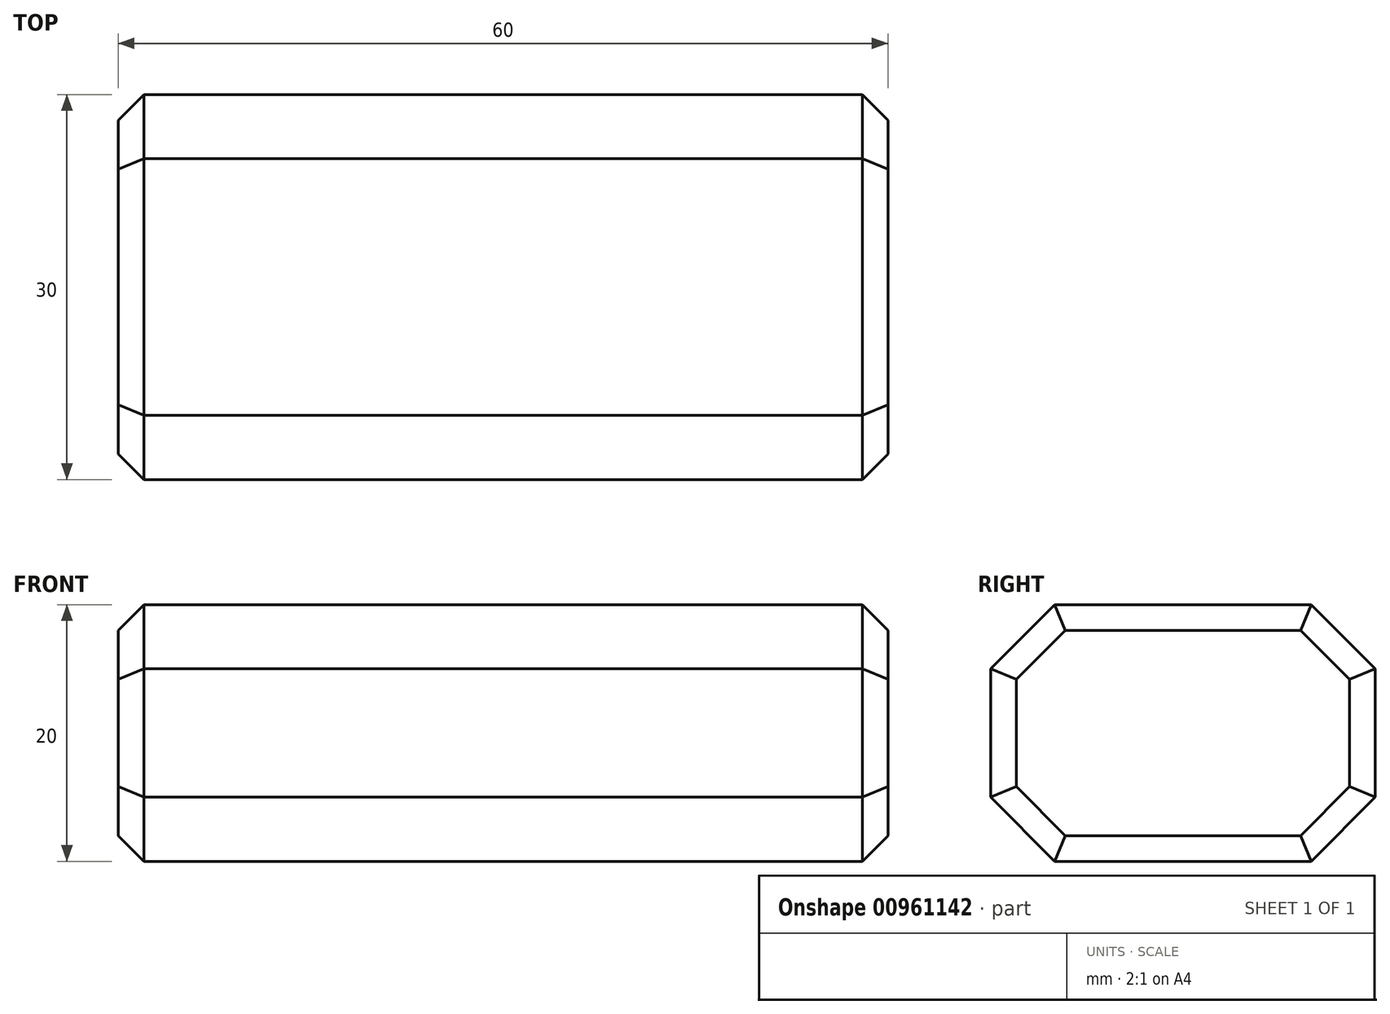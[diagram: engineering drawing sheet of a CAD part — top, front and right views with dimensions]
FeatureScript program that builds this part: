
annotation { "Feature Type Name" : "Feature", "Feature Type Description" : "" }
export const myFeature = defineFeature(function(context is Context, id is Id, definition is map)
    precondition{}
    {
        {
            var Q0;
            Q0=qCreatedBy(makeId("Top.planeOp"),FACE);
            var sketch = newSketch(context, id + "F0", { "sketchPlane" : qUnion([Q0])});
            skLineSegment(sketch, "E0.bottom", {"start": v(-30, 15) * mm, "end": v(30, 15) * mm});
            skLineSegment(sketch, "E0.top", {"start": v(-30, -15) * mm, "end": v(30, -15) * mm});
            skLineSegment(sketch, "E0.left", {"start": v(-30, 15) * mm, "end": v(-30, -15) * mm});
            skLineSegment(sketch, "E0.right", {"start": v(30, 15) * mm, "end": v(30, -15) * mm});
            skLineSegment(sketch, "E1", {"start": v(-30, 0) * mm, "end": v(30, 0) * mm, "construction": true});
            skLineSegment(sketch, "E2", {"start": v(0, 15) * mm, "end": v(0, -15) * mm, "construction": true});
            skPoint(sketch, "E3", {"position": v(0, 0) * mm});
            skSolve(sketch);
        }
        {
            var Q0;
            Q0=qSketchRegion(id+"F0",true);
            extrude(context, id + "F1", {"entities" : qUnion([Q0]), "depth" : 20 * mm, "offsetDistance" : 25 * mm});
        }
        {
            var Q0;
            Q0=makeQuery(id+"F1.opExtrude","CAP_EDGE",EDGE,{"disambiguationData":[OSD([sQuery(id+"F0.wireOp",EDGE,"E0.top")])],"isStart":false});
            var Q1;
            Q1=makeQuery(id+"F1.opExtrude","CAP_EDGE",EDGE,{"disambiguationData":[OSD([sQuery(id+"F0.wireOp",EDGE,"E0.bottom")])],"isStart":false});
            var Q2;
            Q2=makeQuery(id+"F1.opExtrude","CAP_EDGE",EDGE,{"disambiguationData":[OSD([sQuery(id+"F0.wireOp",EDGE,"E0.top")])],"isStart":true});
            var Q3;
            Q3=makeQuery(id+"F1.opExtrude","CAP_EDGE",EDGE,{"disambiguationData":[OSD([sQuery(id+"F0.wireOp",EDGE,"E0.bottom")])],"isStart":true});
            chamfer(context, id + "F2", {"entities" : qUnion([Q0, Q1, Q2, Q3]), "width" : 5 * mm, "tangentPropagation" : true});
        }
        {
            var Q0;
            Q0=makeQuery(id+"F1.opExtrude","SWEPT_FACE",FACE,{"disambiguationData":[OSD([sQuery(id+"F0.wireOp",EDGE,"E0.right")])]});
            var Q1;
            Q1=makeQuery(id+"F1.opExtrude","SWEPT_FACE",FACE,{"disambiguationData":[OSD([sQuery(id+"F0.wireOp",EDGE,"E0.left")])]});
            chamfer(context, id + "F3", {"entities" : qUnion([Q0, Q1]), "width" : 2 * mm, "tangentPropagation" : true});
        }
    });
